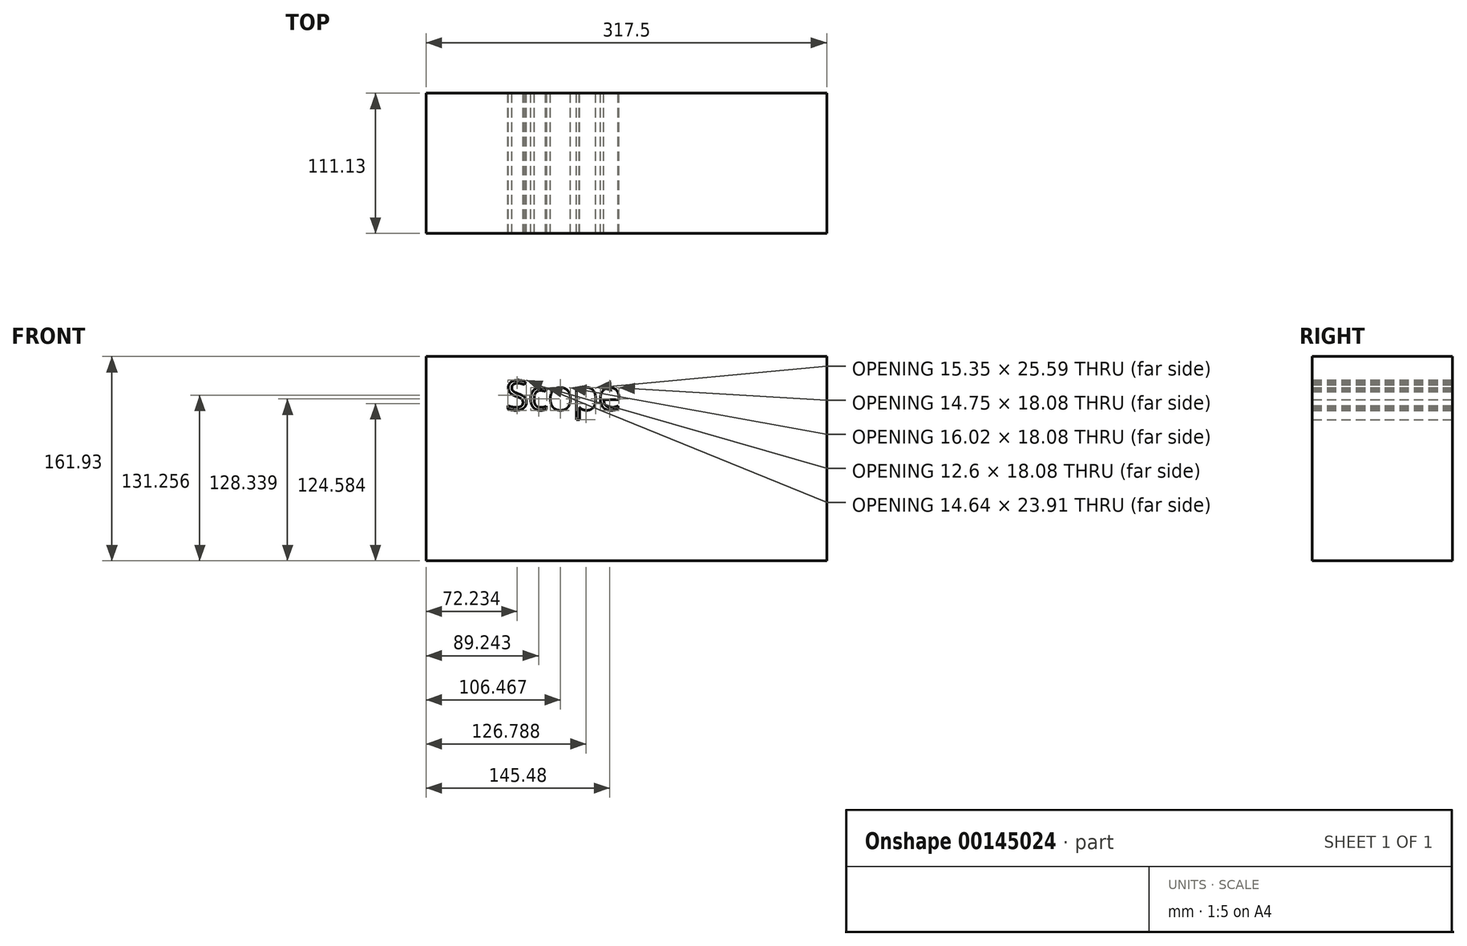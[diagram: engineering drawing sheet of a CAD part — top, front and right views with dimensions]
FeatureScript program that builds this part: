
annotation { "Feature Type Name" : "Feature", "Feature Type Description" : "" }
export const myFeature = defineFeature(function(context is Context, id is Id, definition is map)
    precondition{}
    {
        {
            var Q0;
            Q0=qCreatedBy(makeId("Front.planeOp"),FACE);
            var sketch = newSketch(context, id + "F0", { "sketchPlane" : qUnion([Q0])});
            skLineSegment(sketch, "E0.bottom", {"start": v(-154.96, -64.9) * mm, "end": v(162.54, -64.9) * mm});
            skLineSegment(sketch, "E0.top", {"start": v(-154.96, 97.03) * mm, "end": v(162.54, 97.03) * mm});
            skLineSegment(sketch, "E0.left", {"start": v(-154.96, -64.9) * mm, "end": v(-154.96, 97.03) * mm});
            skLineSegment(sketch, "E0.right", {"start": v(162.54, -64.9) * mm, "end": v(162.54, 97.03) * mm});
            skText(sketch, "E1", { "text": "Scope", "fontName": "OpenSans-Regular.ttf"});
            const initialGuessF0  = {"E1": [-0.09173, 0.05472, 1, 0, 0.02346]};
            skSetInitialGuess(sketch, initialGuessF0);
            skSolve(sketch);
        }
        {
            var Q0;
            Q0=makeQuery(id+"F0.imprint","IMPRINT",FACE,{"disambiguationData":[TD([[makeQuery(id+"F0.imprint","IMPRINT",EDGE,{"derivedFrom":sQuery(id+"F0.wireOp",EDGE,"E0.bottom")}),1.0]])]});
            extrude(context, id + "F1", {"entities" : qUnion([Q0]), "depth" : 111.12 * mm});
        }
    });
